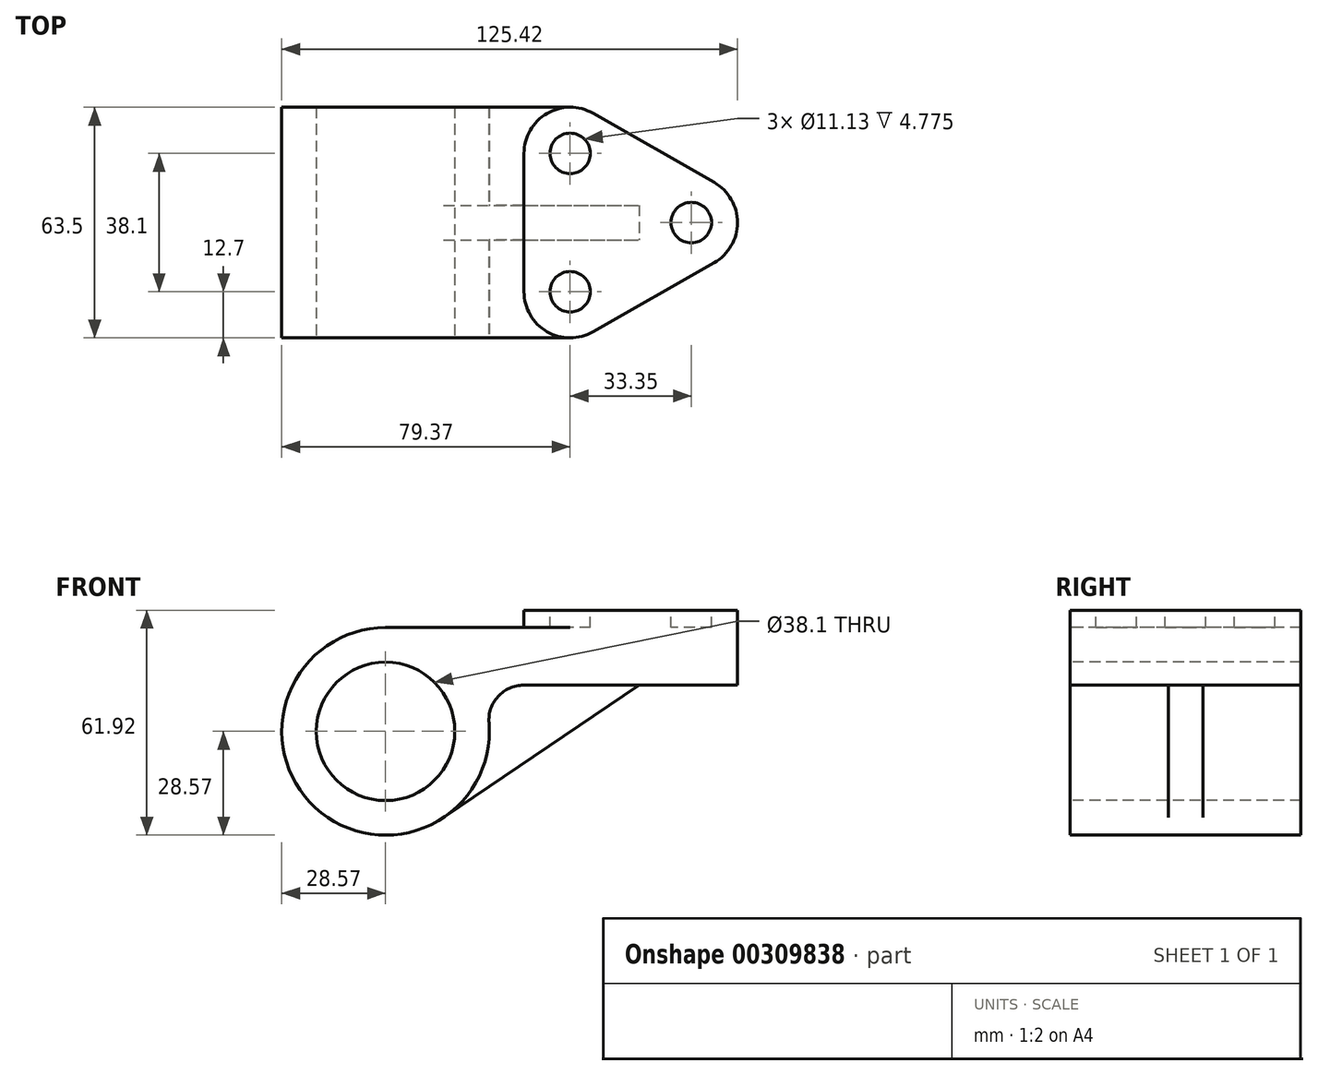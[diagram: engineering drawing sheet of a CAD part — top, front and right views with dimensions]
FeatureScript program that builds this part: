
annotation { "Feature Type Name" : "Feature", "Feature Type Description" : "" }
export const myFeature = defineFeature(function(context is Context, id is Id, definition is map)
    precondition{}
    {
        {
            var Q0;
            Q0=qCreatedBy(makeId("Front.planeOp"),FACE);
            var sketch = newSketch(context, id + "F0", { "sketchPlane" : qUnion([Q0])});
            skCircle(sketch, "E0", {"center": v(0, 0) * mm, "radius": 19.05 * mm});
            skLineSegment(sketch, "E1", {"start": v(0, 28.58) * mm, "end": v(38.1, 28.58) * mm});
            skArc(sketch, "E2", {"start": v(37.97, 12.7) * mm, "mid": v(30.96, 9.62) * mm, "end": v(28.48, 2.38) * mm});
            skArc(sketch, "E3", {"start": v(0, 28.58) * mm, "mid": v(-19.35, -21.03) * mm, "end": v(28.48, 2.38) * mm});
            skLineSegment(sketch, "E4", {"start": v(37.97, 12.7) * mm, "end": v(96.85, 12.7) * mm});
            skLineSegment(sketch, "E5", {"start": v(16, -23.68) * mm, "end": v(69.85, 12.7) * mm});
            skLineSegment(sketch, "E6", {"start": v(38.1, 28.58) * mm, "end": v(38.1, 33.35) * mm});
            skLineSegment(sketch, "E7", {"start": v(38.1, 33.35) * mm, "end": v(96.85, 33.35) * mm});
            skLineSegment(sketch, "E8", {"start": v(96.85, 33.35) * mm, "end": v(96.85, 12.7) * mm});
            skSolve(sketch);
        }
        {
            var Q0;
            Q0=makeQuery(id+"F0.imprint","IMPRINT",FACE,{"disambiguationData":[TD([[makeQuery(id+"F0.imprint","IMPRINT",EDGE,{"derivedFrom":sQuery(id+"F0.wireOp",EDGE,"E0")}),-1.0]])]});
            extrude(context, id + "F1", {"entities" : qUnion([Q0]), "oppositeDirection" : true, "depth" : 63.5 * mm});
        }
        {
            var Q0;
            {var subQ0=sQuery(id+"F0.wireOp",EDGE,"E2");Q0=makeQuery(id+"F0.imprint","IMPRINT",FACE,{"disambiguationData":[TD([[makeQuery(id+"F0.imprint","IMPRINT",EDGE,{"derivedFrom":subQ0}),1.0]])]});}
            extrude(context, id + "F2", {"entities" : qUnion([Q0]), "operationType" : NewBodyOperationType.ADD, "oppositeDirection" : true, "depth" : 36.5 * mm, "hasSecondDirection" : true, "secondDirectionOppositeDirection" : true, "secondDirectionDepth" : 26.99 * mm});
        }
        {
            var Q0;
            Q0=makeQuery(id+"F1.opExtrude","SWEPT_FACE",FACE,{"disambiguationData":[OSD([sQuery(id+"F0.wireOp",EDGE,"E7")])]});
            var sketch = newSketch(context, id + "F3", { "sketchPlane" : qUnion([Q0])});
            skCircle(sketch, "E9", {"center": v(50.8, 50.8) * mm, "radius": 5.56 * mm});
            skCircle(sketch, "E10", {"center": v(50.8, 12.7) * mm, "radius": 5.56 * mm});
            skCircle(sketch, "E11", {"center": v(84.15, 31.75) * mm, "radius": 5.56 * mm});
            skArc(sketch, "E12", {"start": v(90.45, 20.72) * mm, "mid": v(96.85, 31.75) * mm, "end": v(90.45, 42.78) * mm});
            skLineSegment(sketch, "E13", {"start": v(90.45, 42.78) * mm, "end": v(57.1, 61.83) * mm});
            skLineSegment(sketch, "E14", {"start": v(90.45, 20.72) * mm, "end": v(57.1, 1.67) * mm});
            skArc(sketch, "E15", {"start": v(38.1, 12.7) * mm, "mid": v(44.42, 1.72) * mm, "end": v(57.1, 1.67) * mm});
            skArc(sketch, "E16", {"start": v(57.1, 61.83) * mm, "mid": v(44.42, 61.78) * mm, "end": v(38.1, 50.8) * mm});
            skSolve(sketch);
        }
        {
            var Q0;
            {var subQ0=sQuery(id+"F3.wireOp",EDGE,"E15");var subQ1=sQuery(id+"F0.wireOp",EDGE,"E7");var subQ4=makeQuery(id+"F1.opExtrude","CAP_EDGE",EDGE,{"disambiguationData":[OSD([subQ1])],"isStart":true});var subQ5=makeQuery(id+"F3.imprint","INTERSECT",VERTEX,{"derivedFrom":[subQ4,subQ0]});Q0=makeQuery(id+"F3.imprint","IMPRINT",FACE,{"disambiguationData":[TD([[makeQuery(id+"F3.imprint","IMPRINT",EDGE,{"disambiguationData":[TD([[subQ5,1.0]])],"derivedFrom":subQ0}),-1.0]])]});}
            var Q1;
            {var subQ0=sQuery(id+"F3.wireOp",EDGE,"E16");var subQ1=sQuery(id+"F0.wireOp",EDGE,"E7");var subQ4=makeQuery(id+"F1.opExtrude","CAP_EDGE",EDGE,{"disambiguationData":[OSD([subQ1])],"isStart":false});var subQ5=makeQuery(id+"F3.imprint","INTERSECT",VERTEX,{"derivedFrom":[subQ4,subQ0]});Q1=makeQuery(id+"F3.imprint","IMPRINT",FACE,{"disambiguationData":[TD([[makeQuery(id+"F3.imprint","IMPRINT",EDGE,{"disambiguationData":[TD([[subQ5,-1.0]])],"derivedFrom":subQ0}),-1.0]])]});}
            var Q2;
            Q2=makeQuery(id+"F3.imprint","IMPRINT",FACE,{"disambiguationData":[TD([[makeQuery(id+"F3.imprint","IMPRINT",EDGE,{"derivedFrom":sQuery(id+"F3.wireOp",EDGE,"E10")}),1.0]])]});
            var Q3;
            Q3=makeQuery(id+"F3.imprint","IMPRINT",FACE,{"disambiguationData":[TD([[makeQuery(id+"F3.imprint","IMPRINT",EDGE,{"derivedFrom":sQuery(id+"F3.wireOp",EDGE,"E9")}),1.0]])]});
            var Q4;
            Q4=makeQuery(id+"F3.imprint","IMPRINT",FACE,{"disambiguationData":[TD([[makeQuery(id+"F3.imprint","IMPRINT",EDGE,{"derivedFrom":sQuery(id+"F3.wireOp",EDGE,"E11")}),1.0]])]});
            extrude(context, id + "F4", {"entities" : qUnion([Q0, Q1, Q2, Q3, Q4]), "operationType" : NewBodyOperationType.REMOVE, "oppositeDirection" : true, "depth" : 4.78 * mm});
        }
        {
            var Q0;
            {var subQ6=sQuery(id+"F3.wireOp",EDGE,"E14");Q0=makeQuery(id+"F3.imprint","IMPRINT",FACE,{"disambiguationData":[TD([[makeQuery(id+"F3.imprint","IMPRINT",EDGE,{"derivedFrom":subQ6}),1.0]])]});}
            var Q1;
            {var subQ6=sQuery(id+"F3.wireOp",EDGE,"E13");Q1=makeQuery(id+"F3.imprint","IMPRINT",FACE,{"disambiguationData":[TD([[makeQuery(id+"F3.imprint","IMPRINT",EDGE,{"derivedFrom":subQ6}),-1.0]])]});}
            extrude(context, id + "F5", {"entities" : qUnion([Q0, Q1]), "operationType" : NewBodyOperationType.REMOVE, "oppositeDirection" : true, "depth" : 25.4 * mm});
        }
    });
